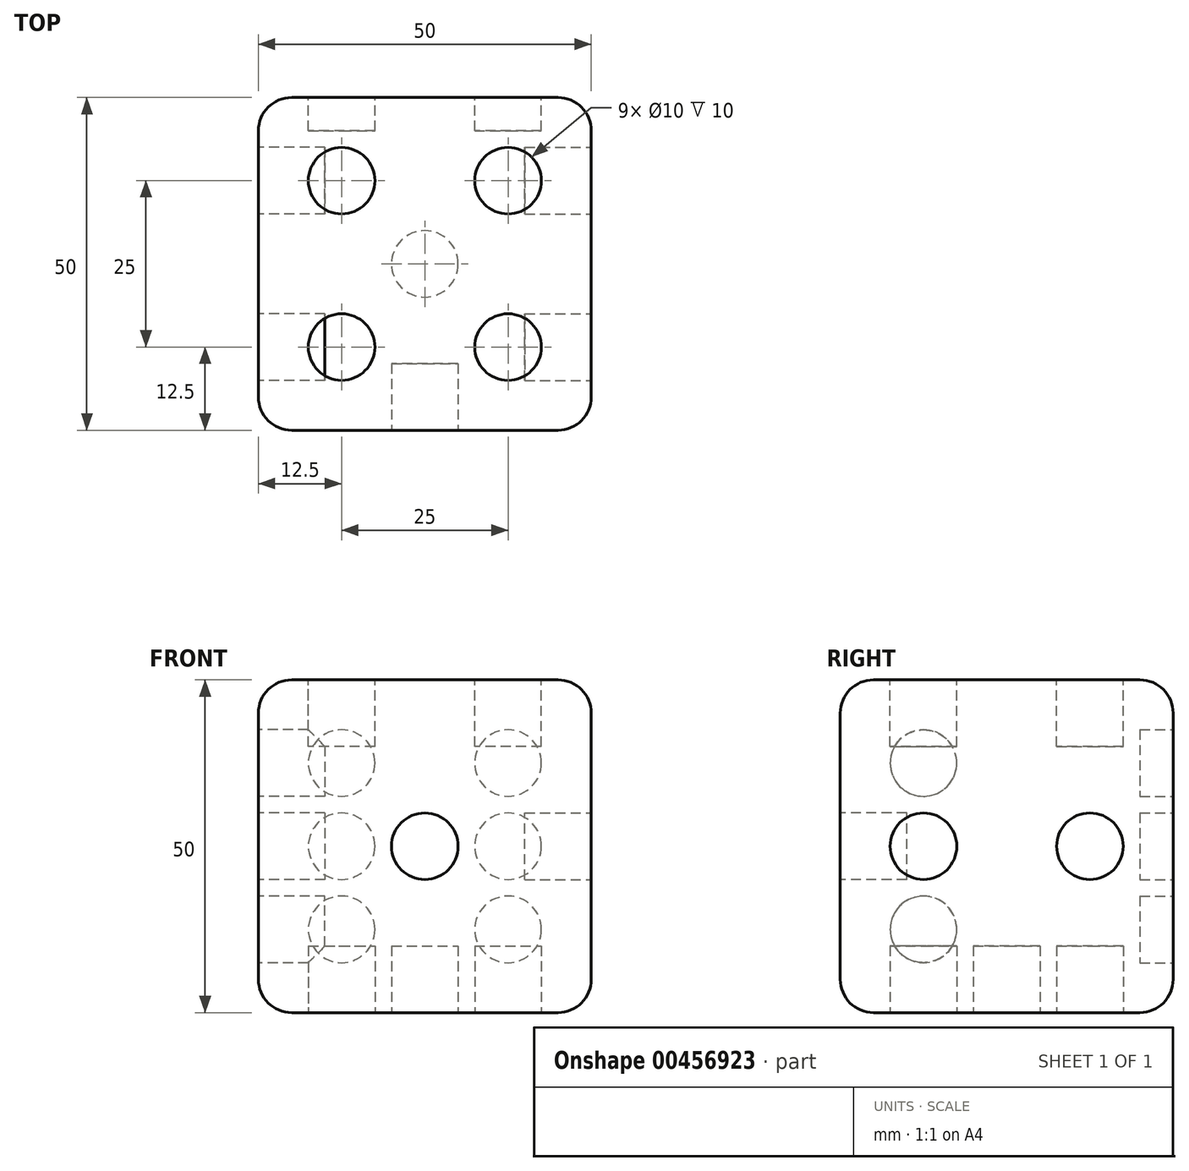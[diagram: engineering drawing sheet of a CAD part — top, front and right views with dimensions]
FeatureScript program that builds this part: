
annotation { "Feature Type Name" : "Feature", "Feature Type Description" : "" }
export const myFeature = defineFeature(function(context is Context, id is Id, definition is map)
    precondition{}
    {
        {
            var Q0;
            Q0=qCreatedBy(makeId("Front.planeOp"),FACE);
            var sketch = newSketch(context, id + "F0", { "sketchPlane" : qUnion([Q0])});
            skLineSegment(sketch, "E0.bottom", {"start": v(-25, 25) * mm, "end": v(25, 25) * mm});
            skLineSegment(sketch, "E0.top", {"start": v(-25, -25) * mm, "end": v(25, -25) * mm});
            skLineSegment(sketch, "E0.left", {"start": v(-25, 25) * mm, "end": v(-25, -25) * mm});
            skLineSegment(sketch, "E0.right", {"start": v(25, 25) * mm, "end": v(25, -25) * mm});
            skPoint(sketch, "E0.middle", {"position": v(0, 0) * mm});
            skSolve(sketch);
        }
        {
            var Q0;
            Q0=makeQuery(id+"F0.imprint","IMPRINT",FACE,{"disambiguationData":[TD([[makeQuery(id+"F0.imprint","IMPRINT",EDGE,{"derivedFrom":sQuery(id+"F0.wireOp",EDGE,"E0.bottom")}),-1.0]])]});
            extrude(context, id + "F1", {"entities" : qUnion([Q0]), "depth" : 50 * mm});
        }
        {
            var Q0;
            Q0=makeQuery(id+"F1.opExtrude","CAP_FACE",FACE,{"disambiguationData":[OSD([sQuery(id+"F0.wireOp",EDGE,"E0.bottom"),sQuery(id+"F0.wireOp",EDGE,"E0.top"),sQuery(id+"F0.wireOp",EDGE,"E0.left"),sQuery(id+"F0.wireOp",EDGE,"E0.right")])],"isStart":false});
            var sketch = newSketch(context, id + "F2", { "sketchPlane" : qUnion([Q0])});
            skCircle(sketch, "E1", {"center": v(0, 0) * mm, "radius": 5 * mm});
            skSolve(sketch);
        }
        {
            var Q0;
            Q0=makeQuery(id+"F2.imprint","IMPRINT",FACE,{"disambiguationData":[TD([[makeQuery(id+"F2.imprint","IMPRINT",EDGE,{"derivedFrom":sQuery(id+"F2.wireOp",EDGE,"E1")}),1.0]])]});
            extrude(context, id + "F3", {"entities" : qUnion([Q0]), "operationType" : NewBodyOperationType.REMOVE, "oppositeDirection" : true, "depth" : 10 * mm});
        }
        {
            var Q0;
            Q0=makeQuery(id+"F1.opExtrude","CAP_FACE",FACE,{"disambiguationData":[OSD([sQuery(id+"F0.wireOp",EDGE,"E0.bottom"),sQuery(id+"F0.wireOp",EDGE,"E0.top"),sQuery(id+"F0.wireOp",EDGE,"E0.left"),sQuery(id+"F0.wireOp",EDGE,"E0.right")])],"isStart":true});
            var sketch = newSketch(context, id + "F4", { "sketchPlane" : qUnion([Q0])});
            skLineSegment(sketch, "E2", {"start": v(0, -25) * mm, "end": v(0, 25) * mm, "construction": true});
            skLineSegment(sketch, "E3", {"start": v(25, 0) * mm, "end": v(-25, 0) * mm, "construction": true});
            skSolve(sketch);
        }
        {
            var Q0;
            Q0=makeQuery(id+"F4.imprint","IMPRINT",FACE,{"disambiguationData":[TD([[makeQuery(id+"F4.imprint","IMPRINT",EDGE,{"derivedFrom":makeQuery(id+"F1.opExtrude","CAP_EDGE",EDGE,{"disambiguationData":[OSD([sQuery(id+"F0.wireOp",EDGE,"E0.bottom")])],"isStart":true})}),1.0]])]});
            var sketch = newSketch(context, id + "F5", { "sketchPlane" : qUnion([Q0])});
            skPoint(sketch, "E4.0", {"position": v(25, -25) * mm});
            skPoint(sketch, "E5.0", {"position": v(-25, 25) * mm});
            skPoint(sketch, "E6.0", {"position": v(-25, -25) * mm});
            skPoint(sketch, "E7.0", {"position": v(25, 25) * mm});
            skPoint(sketch, "E8.0", {"position": v(25, 0) * mm});
            skPoint(sketch, "E9.0", {"position": v(0, -25) * mm});
            skPoint(sketch, "E10.0", {"position": v(-25, 0) * mm});
            skPoint(sketch, "E11.0", {"position": v(0, 25) * mm});
            skLineSegment(sketch, "E12", {"start": v(25, -25) * mm, "end": v(-25, 25) * mm, "construction": true});
            skLineSegment(sketch, "E13", {"start": v(25, 25) * mm, "end": v(-25, -25) * mm, "construction": true});
            skCircle(sketch, "E14", {"center": v(12.5, -12.5) * mm, "radius": 5 * mm});
            skCircle(sketch, "E15", {"center": v(12.5, 0) * mm, "radius": 5 * mm});
            skCircle(sketch, "E16", {"center": v(12.5, 12.5) * mm, "radius": 5 * mm});
            skLineSegment(sketch, "E17", {"start": v(0, -25) * mm, "end": v(0, 25) * mm});
            skCircle(sketch, "E18.1.0.0", {"center": v(-12.5, -12.5) * mm, "radius": 5 * mm});
            skCircle(sketch, "E18.1.0.1", {"center": v(-12.5, 0) * mm, "radius": 5 * mm});
            skCircle(sketch, "E18.1.0.2", {"center": v(-12.5, 12.5) * mm, "radius": 5 * mm});
            skLineSegment(sketch, "E18.direction1", {"start": v(12.5, -12.5) * mm, "end": v(-12.5, -12.5) * mm, "construction": true});
            skSolve(sketch);
        }
        {
            var Q0;
            Q0=makeQuery(id+"F1.opExtrude","SWEPT_FACE",FACE,{"disambiguationData":[OSD([sQuery(id+"F0.wireOp",EDGE,"E0.right")])]});
            var sketch = newSketch(context, id + "F6", { "sketchPlane" : qUnion([Q0])});
            skPoint(sketch, "E19.0", {"position": v(0, 0) * mm});
            skPoint(sketch, "E20.0", {"position": v(-50, 0) * mm});
            skPoint(sketch, "E21.0", {"position": v(-25, -25) * mm});
            skPoint(sketch, "E22.0", {"position": v(-25, 25) * mm});
            skLineSegment(sketch, "E23", {"start": v(0, 0) * mm, "end": v(-50, 0) * mm, "construction": true});
            skLineSegment(sketch, "E24", {"start": v(-25, -25) * mm, "end": v(-25, 25) * mm, "construction": true});
            skCircle(sketch, "E25", {"center": v(-12.5, 0) * mm, "radius": 5 * mm});
            skCircle(sketch, "E26.1.0.0", {"center": v(-37.5, 0) * mm, "radius": 5 * mm});
            skLineSegment(sketch, "E26.direction1", {"start": v(-12.5, 0) * mm, "end": v(-37.5, 0) * mm, "construction": true});
            skSolve(sketch);
        }
        {
            var Q0;
            Q0=makeQuery(id+"F6.imprint","IMPRINT",FACE,{"disambiguationData":[TD([[makeQuery(id+"F6.imprint","IMPRINT",EDGE,{"derivedFrom":sQuery(id+"F6.wireOp",EDGE,"E25")}),1.0]])]});
            var Q1;
            Q1=makeQuery(id+"F6.imprint","IMPRINT",FACE,{"disambiguationData":[TD([[makeQuery(id+"F6.imprint","IMPRINT",EDGE,{"derivedFrom":sQuery(id+"F6.wireOp",EDGE,"E26.1.0.0")}),1.0]])]});
            var Q2;
            Q2=sQuery(id+"F6.wireOp",EDGE,"E26.1.0.0");
            var Q3;
            Q3=sQuery(id+"F6.wireOp",EDGE,"E25");
            extrude(context, id + "F7", {"entities" : qUnion([Q0, Q1]), "operationType" : NewBodyOperationType.REMOVE, "surfaceEntities" : qUnion([Q2, Q3]), "oppositeDirection" : true, "depth" : 10 * mm});
        }
        {
            var Q0;
            Q0=makeQuery(id+"F5.imprint","IMPRINT",FACE,{"disambiguationData":[TD([[makeQuery(id+"F5.imprint","IMPRINT",EDGE,{"derivedFrom":sQuery(id+"F5.wireOp",EDGE,"E14")}),1.0]])]});
            var Q1;
            Q1=makeQuery(id+"F5.imprint","IMPRINT",FACE,{"disambiguationData":[TD([[makeQuery(id+"F5.imprint","IMPRINT",EDGE,{"derivedFrom":sQuery(id+"F5.wireOp",EDGE,"E15")}),1.0]])]});
            var Q2;
            Q2=makeQuery(id+"F5.imprint","IMPRINT",FACE,{"disambiguationData":[TD([[makeQuery(id+"F5.imprint","IMPRINT",EDGE,{"derivedFrom":sQuery(id+"F5.wireOp",EDGE,"E16")}),1.0]])]});
            var Q3;
            Q3=makeQuery(id+"F5.imprint","IMPRINT",FACE,{"disambiguationData":[TD([[makeQuery(id+"F5.imprint","IMPRINT",EDGE,{"derivedFrom":sQuery(id+"F5.wireOp",EDGE,"E18.1.0.0")}),1.0]])]});
            var Q4;
            Q4=makeQuery(id+"F5.imprint","IMPRINT",FACE,{"disambiguationData":[TD([[makeQuery(id+"F5.imprint","IMPRINT",EDGE,{"derivedFrom":sQuery(id+"F5.wireOp",EDGE,"E18.1.0.1")}),1.0]])]});
            var Q5;
            Q5=makeQuery(id+"F5.imprint","IMPRINT",FACE,{"disambiguationData":[TD([[makeQuery(id+"F5.imprint","IMPRINT",EDGE,{"derivedFrom":sQuery(id+"F5.wireOp",EDGE,"E18.1.0.2")}),1.0]])]});
            var Q6;
            Q6=sQuery(id+"F5.wireOp",EDGE,"E14");
            var Q7;
            Q7=sQuery(id+"F5.wireOp",EDGE,"E18.1.0.0");
            var Q8;
            Q8=sQuery(id+"F5.wireOp",EDGE,"E18.1.0.1");
            var Q9;
            Q9=sQuery(id+"F5.wireOp",EDGE,"E15");
            var Q10;
            Q10=sQuery(id+"F5.wireOp",EDGE,"E16");
            var Q11;
            Q11=sQuery(id+"F5.wireOp",EDGE,"E18.1.0.2");
            extrude(context, id + "F8", {"entities" : qUnion([Q0, Q1, Q2, Q3, Q4, Q5]), "operationType" : NewBodyOperationType.REMOVE, "surfaceEntities" : qUnion([Q6, Q7, Q8, Q9, Q10, Q11]), "oppositeDirection" : true, "depth" : 5 * mm});
        }
        {
            var Q0;
            Q0=makeQuery(id+"F1.opExtrude","SWEPT_FACE",FACE,{"disambiguationData":[OSD([sQuery(id+"F0.wireOp",EDGE,"E0.left")])]});
            var sketch = newSketch(context, id + "F9", { "sketchPlane" : qUnion([Q0])});
            skPoint(sketch, "E27.0", {"position": v(50, -25) * mm});
            skPoint(sketch, "E28.0", {"position": v(50, 25) * mm});
            skLineSegment(sketch, "E29", {"start": v(0, 0) * mm, "end": v(50, 0) * mm, "construction": true});
            skLineSegment(sketch, "E30", {"start": v(50, 0) * mm, "end": v(50, -25) * mm, "construction": true});
            skLineSegment(sketch, "E31", {"start": v(25, 0) * mm, "end": v(50, -25) * mm, "construction": true});
            skLineSegment(sketch, "E32", {"start": v(25, 0) * mm, "end": v(50, 25) * mm, "construction": true});
            skCircle(sketch, "E33", {"center": v(12.5, 0) * mm, "radius": 5 * mm});
            skPoint(sketch, "E34.0", {"position": v(25, -25) * mm});
            skPoint(sketch, "E35.0", {"position": v(25, 25) * mm});
            skLineSegment(sketch, "E36", {"start": v(25, -25) * mm, "end": v(50, 0) * mm, "construction": true});
            skLineSegment(sketch, "E37", {"start": v(50, 0) * mm, "end": v(25, 25) * mm, "construction": true});
            skCircle(sketch, "E38", {"center": v(37.5, -12.5) * mm, "radius": 5 * mm});
            skCircle(sketch, "E39", {"center": v(37.5, 12.5) * mm, "radius": 5 * mm});
            skSolve(sketch);
        }
        {
            var Q0;
            Q0=makeQuery(id+"F9.imprint","IMPRINT",FACE,{"disambiguationData":[TD([[makeQuery(id+"F9.imprint","IMPRINT",EDGE,{"derivedFrom":sQuery(id+"F9.wireOp",EDGE,"E33")}),1.0]])]});
            var Q1;
            Q1=makeQuery(id+"F9.imprint","IMPRINT",FACE,{"disambiguationData":[TD([[makeQuery(id+"F9.imprint","IMPRINT",EDGE,{"derivedFrom":sQuery(id+"F9.wireOp",EDGE,"E38")}),1.0]])]});
            var Q2;
            Q2=makeQuery(id+"F9.imprint","IMPRINT",FACE,{"disambiguationData":[TD([[makeQuery(id+"F9.imprint","IMPRINT",EDGE,{"derivedFrom":sQuery(id+"F9.wireOp",EDGE,"E39")}),1.0]])]});
            extrude(context, id + "F10", {"entities" : qUnion([Q0, Q1, Q2]), "operationType" : NewBodyOperationType.REMOVE, "oppositeDirection" : true, "depth" : 10 * mm});
        }
        {
            var Q0;
            Q0=makeQuery(id+"F1.opExtrude","SWEPT_FACE",FACE,{"disambiguationData":[OSD([sQuery(id+"F0.wireOp",EDGE,"E0.bottom")])]});
            var sketch = newSketch(context, id + "F11", { "sketchPlane" : qUnion([Q0])});
            skPoint(sketch, "E40.0", {"position": v(-25, -50) * mm});
            skPoint(sketch, "E41.0", {"position": v(0, -50) * mm});
            skPoint(sketch, "E42.0", {"position": v(25, -50) * mm});
            skPoint(sketch, "E43.0", {"position": v(25, -25) * mm});
            skPoint(sketch, "E44.0", {"position": v(25, 0) * mm});
            skPoint(sketch, "E45.0", {"position": v(-25, 0) * mm});
            skPoint(sketch, "E46.0", {"position": v(-25, -25) * mm});
            skLineSegment(sketch, "E47.0", {"start": v(-25, 0) * mm, "end": v(25, 0) * mm});
            skLineSegment(sketch, "E48", {"start": v(-25, -50) * mm, "end": v(25, 0) * mm, "construction": true});
            skLineSegment(sketch, "E49", {"start": v(25, -50) * mm, "end": v(-25, 0) * mm, "construction": true});
            skLineSegment(sketch, "E50", {"start": v(0, -50) * mm, "end": v(0, 0) * mm, "construction": true});
            skLineSegment(sketch, "E51", {"start": v(-25, -25) * mm, "end": v(25, -25) * mm, "construction": true});
            skLineSegment(sketch, "E52", {"start": v(0, -50) * mm, "end": v(-25, -25) * mm, "construction": true});
            skLineSegment(sketch, "E53", {"start": v(-25, -25) * mm, "end": v(0, 0) * mm, "construction": true});
            skLineSegment(sketch, "E54", {"start": v(0, 0) * mm, "end": v(25, -25) * mm, "construction": true});
            skLineSegment(sketch, "E55", {"start": v(25, -25) * mm, "end": v(0, -50) * mm, "construction": true});
            skCircle(sketch, "E56", {"center": v(-12.5, -37.5) * mm, "radius": 5 * mm});
            skCircle(sketch, "E57", {"center": v(-12.5, -12.5) * mm, "radius": 5 * mm});
            skCircle(sketch, "E58", {"center": v(12.5, -37.5) * mm, "radius": 5 * mm});
            skCircle(sketch, "E59", {"center": v(12.5, -12.5) * mm, "radius": 5 * mm});
            skSolve(sketch);
        }
        {
            var Q0;
            Q0=makeQuery(id+"F11.imprint","IMPRINT",FACE,{"disambiguationData":[TD([[makeQuery(id+"F11.imprint","IMPRINT",EDGE,{"derivedFrom":sQuery(id+"F11.wireOp",EDGE,"E56")}),1.0]])]});
            var Q1;
            Q1=makeQuery(id+"F11.imprint","IMPRINT",FACE,{"disambiguationData":[TD([[makeQuery(id+"F11.imprint","IMPRINT",EDGE,{"derivedFrom":sQuery(id+"F11.wireOp",EDGE,"E57")}),1.0]])]});
            var Q2;
            Q2=makeQuery(id+"F11.imprint","IMPRINT",FACE,{"disambiguationData":[TD([[makeQuery(id+"F11.imprint","IMPRINT",EDGE,{"derivedFrom":sQuery(id+"F11.wireOp",EDGE,"E59")}),1.0]])]});
            var Q3;
            Q3=makeQuery(id+"F11.imprint","IMPRINT",FACE,{"disambiguationData":[TD([[makeQuery(id+"F11.imprint","IMPRINT",EDGE,{"derivedFrom":sQuery(id+"F11.wireOp",EDGE,"E58")}),1.0]])]});
            extrude(context, id + "F12", {"entities" : qUnion([Q0, Q1, Q2, Q3]), "operationType" : NewBodyOperationType.REMOVE, "oppositeDirection" : true, "depth" : 10 * mm});
        }
        {
            var Q0;
            Q0=makeQuery(id+"F1.opExtrude","SWEPT_FACE",FACE,{"disambiguationData":[OSD([sQuery(id+"F0.wireOp",EDGE,"E0.top")])]});
            var sketch = newSketch(context, id + "F13", { "sketchPlane" : qUnion([Q0])});
            skPoint(sketch, "E60.0", {"position": v(-25, 25) * mm});
            skPoint(sketch, "E61.0", {"position": v(-25, 0) * mm});
            skPoint(sketch, "E62.0", {"position": v(25, 0) * mm});
            skPoint(sketch, "E63.0", {"position": v(25, 25) * mm});
            skPoint(sketch, "E64.0", {"position": v(25, 50) * mm});
            skPoint(sketch, "E65.0", {"position": v(0, 50) * mm});
            skPoint(sketch, "E66.0", {"position": v(-25, 50) * mm});
            skLineSegment(sketch, "E67", {"start": v(-25, 0) * mm, "end": v(25, 50) * mm, "construction": true});
            skLineSegment(sketch, "E68", {"start": v(25, 0) * mm, "end": v(-25, 50) * mm, "construction": true});
            skLineSegment(sketch, "E69", {"start": v(-25, 25) * mm, "end": v(25, 25) * mm, "construction": true});
            skLineSegment(sketch, "E70", {"start": v(0, 0) * mm, "end": v(0, 50) * mm, "construction": true});
            skLineSegment(sketch, "E71", {"start": v(0, 50) * mm, "end": v(-25, 25) * mm, "construction": true});
            skLineSegment(sketch, "E72", {"start": v(-25, 25) * mm, "end": v(0, 0) * mm, "construction": true});
            skLineSegment(sketch, "E73", {"start": v(0, 0) * mm, "end": v(25, 25) * mm, "construction": true});
            skLineSegment(sketch, "E74", {"start": v(25, 25) * mm, "end": v(0, 50) * mm, "construction": true});
            skCircle(sketch, "E75", {"center": v(-12.5, 12.5) * mm, "radius": 5 * mm});
            skCircle(sketch, "E76", {"center": v(-12.5, 37.5) * mm, "radius": 5 * mm});
            skCircle(sketch, "E77", {"center": v(0, 25) * mm, "radius": 5 * mm});
            skCircle(sketch, "E78", {"center": v(12.5, 12.5) * mm, "radius": 5 * mm});
            skCircle(sketch, "E79", {"center": v(12.5, 37.5) * mm, "radius": 5 * mm});
            skSolve(sketch);
        }
        {
            var Q0;
            Q0=makeQuery(id+"F13.imprint","IMPRINT",FACE,{"disambiguationData":[TD([[makeQuery(id+"F13.imprint","IMPRINT",EDGE,{"derivedFrom":sQuery(id+"F13.wireOp",EDGE,"E76")}),1.0]])]});
            var Q1;
            Q1=makeQuery(id+"F13.imprint","IMPRINT",FACE,{"disambiguationData":[TD([[makeQuery(id+"F13.imprint","IMPRINT",EDGE,{"derivedFrom":sQuery(id+"F13.wireOp",EDGE,"E79")}),1.0]])]});
            var Q2;
            Q2=makeQuery(id+"F13.imprint","IMPRINT",FACE,{"disambiguationData":[TD([[makeQuery(id+"F13.imprint","IMPRINT",EDGE,{"derivedFrom":sQuery(id+"F13.wireOp",EDGE,"E77")}),1.0]])]});
            var Q3;
            Q3=makeQuery(id+"F13.imprint","IMPRINT",FACE,{"disambiguationData":[TD([[makeQuery(id+"F13.imprint","IMPRINT",EDGE,{"derivedFrom":sQuery(id+"F13.wireOp",EDGE,"E75")}),1.0]])]});
            var Q4;
            Q4=makeQuery(id+"F13.imprint","IMPRINT",FACE,{"disambiguationData":[TD([[makeQuery(id+"F13.imprint","IMPRINT",EDGE,{"derivedFrom":sQuery(id+"F13.wireOp",EDGE,"E78")}),1.0]])]});
            var Q5;
            Q5=sQuery(id+"F13.wireOp",EDGE,"E76");
            var Q6;
            Q6=sQuery(id+"F13.wireOp",EDGE,"E79");
            var Q7;
            Q7=sQuery(id+"F13.wireOp",EDGE,"E77");
            var Q8;
            Q8=sQuery(id+"F13.wireOp",EDGE,"E75");
            var Q9;
            Q9=sQuery(id+"F13.wireOp",EDGE,"E78");
            extrude(context, id + "F14", {"entities" : qUnion([Q0, Q1, Q2, Q3, Q4]), "operationType" : NewBodyOperationType.REMOVE, "surfaceEntities" : qUnion([Q5, Q6, Q7, Q8, Q9]), "oppositeDirection" : true, "depth" : 10 * mm});
        }
        {
            var Q0;
            Q0=makeQuery(id+"F1.opExtrude","CAP_EDGE",EDGE,{"disambiguationData":[OSD([sQuery(id+"F0.wireOp",EDGE,"E0.top")])],"isStart":false});
            var Q1;
            Q1=makeQuery(id+"F1.opExtrude","SWEPT_EDGE",EDGE,{"disambiguationData":[OSD([sQuery(id+"F0.wireOp",EDGE,"E0.top"),sQuery(id+"F0.wireOp",EDGE,"E0.right")])]});
            var Q2;
            Q2=makeQuery(id+"F1.opExtrude","CAP_EDGE",EDGE,{"disambiguationData":[OSD([sQuery(id+"F0.wireOp",EDGE,"E0.right")])],"isStart":false});
            var Q3;
            Q3=makeQuery(id+"F1.opExtrude","CAP_EDGE",EDGE,{"disambiguationData":[OSD([sQuery(id+"F0.wireOp",EDGE,"E0.right")])],"isStart":true});
            var Q4;
            Q4=makeQuery(id+"F1.opExtrude","CAP_EDGE",EDGE,{"disambiguationData":[OSD([sQuery(id+"F0.wireOp",EDGE,"E0.top")])],"isStart":true});
            var Q5;
            Q5=makeQuery(id+"F1.opExtrude","SWEPT_EDGE",EDGE,{"disambiguationData":[OSD([sQuery(id+"F0.wireOp",EDGE,"E0.top"),sQuery(id+"F0.wireOp",EDGE,"E0.left")])]});
            var Q6;
            Q6=makeQuery(id+"F1.opExtrude","CAP_EDGE",EDGE,{"disambiguationData":[OSD([sQuery(id+"F0.wireOp",EDGE,"E0.left")])],"isStart":false});
            var Q7;
            Q7=makeQuery(id+"F1.opExtrude","CAP_EDGE",EDGE,{"disambiguationData":[OSD([sQuery(id+"F0.wireOp",EDGE,"E0.left")])],"isStart":true});
            var Q8;
            Q8=makeQuery(id+"F1.opExtrude","CAP_EDGE",EDGE,{"disambiguationData":[OSD([sQuery(id+"F0.wireOp",EDGE,"E0.bottom")])],"isStart":true});
            var Q9;
            Q9=makeQuery(id+"F1.opExtrude","SWEPT_EDGE",EDGE,{"disambiguationData":[OSD([sQuery(id+"F0.wireOp",EDGE,"E0.bottom"),sQuery(id+"F0.wireOp",EDGE,"E0.left")])]});
            var Q10;
            Q10=makeQuery(id+"F1.opExtrude","CAP_EDGE",EDGE,{"disambiguationData":[OSD([sQuery(id+"F0.wireOp",EDGE,"E0.bottom")])],"isStart":false});
            var Q11;
            Q11=makeQuery(id+"F1.opExtrude","SWEPT_EDGE",EDGE,{"disambiguationData":[OSD([sQuery(id+"F0.wireOp",EDGE,"E0.bottom"),sQuery(id+"F0.wireOp",EDGE,"E0.right")])]});
            fillet(context, id + "F15", {"entities" : qUnion([Q0, Q1, Q2, Q3, Q4, Q5, Q6, Q7, Q8, Q9, Q10, Q11]), "radius" : 5 * mm, "tangentPropagation" : true, "allowEdgeOverflow" : false});
        }
    });
